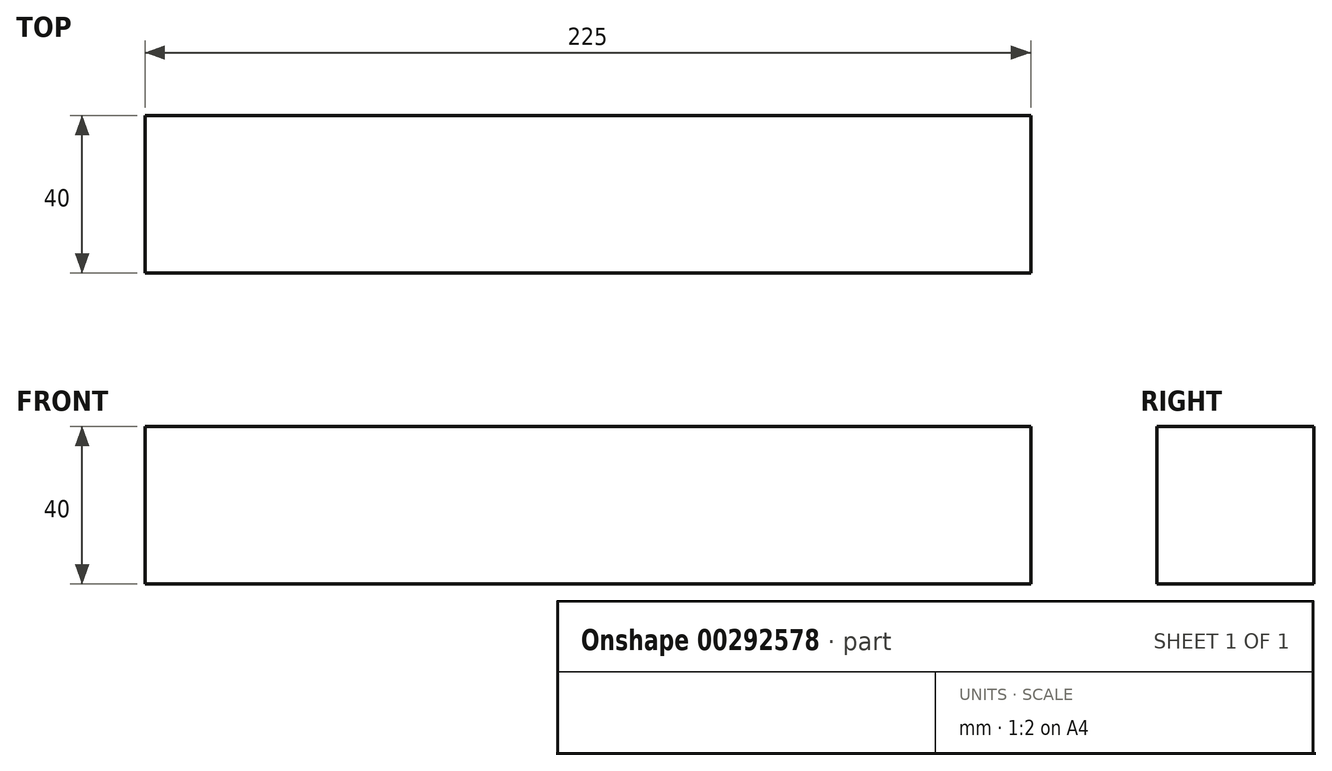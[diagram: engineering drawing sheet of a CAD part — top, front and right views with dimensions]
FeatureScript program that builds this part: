
annotation { "Feature Type Name" : "Feature", "Feature Type Description" : "" }
export const myFeature = defineFeature(function(context is Context, id is Id, definition is map)
    precondition{}
    {
        {
            var Q0;
            Q0=qCreatedBy(makeId("Front.planeOp"),FACE);
            var sketch = newSketch(context, id + "F0", { "sketchPlane" : qUnion([Q0])});
            skLineSegment(sketch, "E0", {"start": v(-112.5, -32.23) * mm, "end": v(112.5, -32.23) * mm});
            skLineSegment(sketch, "E1", {"start": v(112.5, -32.23) * mm, "end": v(112.5, -72.23) * mm});
            skLineSegment(sketch, "E2", {"start": v(112.5, -72.23) * mm, "end": v(-112.5, -72.23) * mm});
            skLineSegment(sketch, "E3", {"start": v(-112.5, -72.23) * mm, "end": v(-112.5, -32.23) * mm});
            skSolve(sketch);
        }
        {
            var Q0;
            Q0 = qSketchRegion(id + "F0", true);
            extrude(context, id + "F1", {"entities" : qUnion([Q0]), "depth" : 40 * mm});
        }
    });
